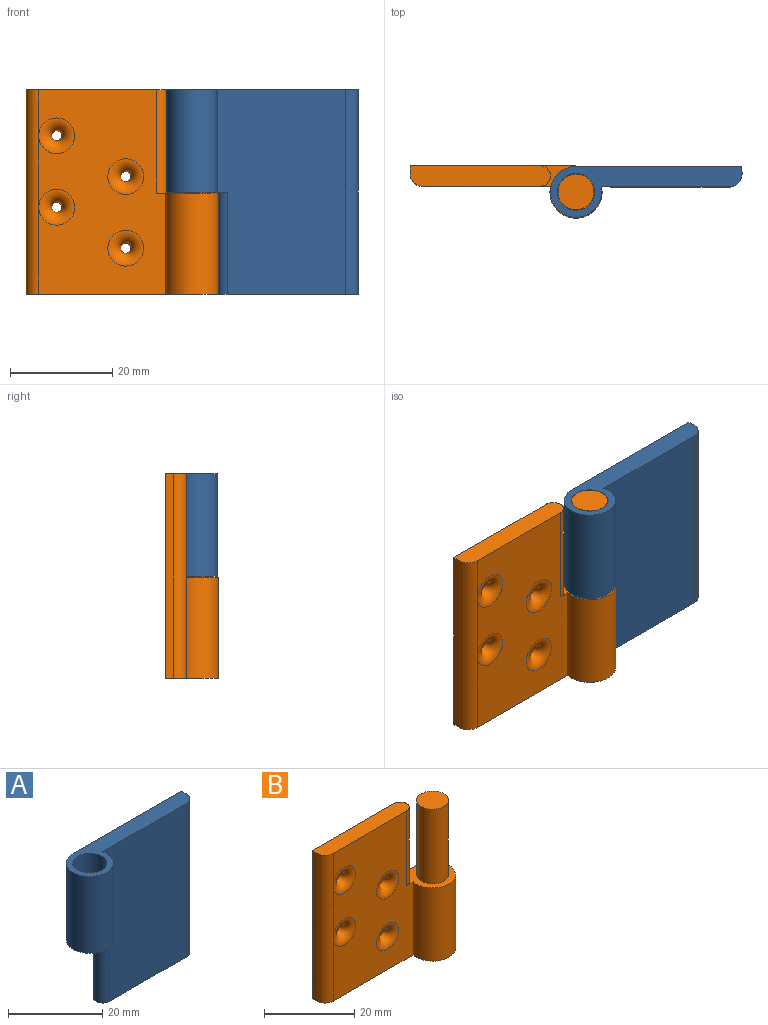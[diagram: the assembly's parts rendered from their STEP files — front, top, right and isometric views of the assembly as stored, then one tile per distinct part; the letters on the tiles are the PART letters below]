
ASSEMBLY  parts=2 mates=1
PART A: 10 faces, bbox 37.5x10x40 mm
  f0: plane 40x32.5mm, normal (0,1,0), area 1162mm2, adj f2,f3,f4,f5,f7,f8
  f1: plane 40x25.1mm, normal (0,-1,0), area 964mm2, adj f3,f4,f5,f7,f8,f9
  f2: plane 40x1.5mm, normal (1,0,0), area 60mm2, adj f0,f3,f4,f9
  f3: plane 37.5x10mm, normal (0,0,1), area 151.8mm2, adj f0,f1,f2,f5,f6,f9
  f4: plane 27.6x4mm, normal (0,0,-1), area 107.3mm2, adj f0,f1,f2,f8,f9
  f5: cylinder r=5mm len=20mm, axis (0,0,-1), area 491.4mm2, adj f0,f1,f3,f7
  f6: cylinder r=3.6mm len=20mm, axis (0,0,-1), area 452.4mm2, adj f3,f7
  f7: plane 11.9x10mm, normal (0,0,-1), area 44.5mm2, adj f0,f1,f5,f6,f8
  f8: cylinder r=2mm len=20mm, axis (0,0,1), area 125.7mm2, adj f0,f1,f4,f7
  f9: cylinder r=2.5mm len=40mm, axis (0,0,1), area 157.1mm2, adj f1,f2,f3,f4
PART B: 19 faces, bbox 37.6x10.2x40 mm
  f0: plane 40x1.5mm, normal (-1,0,0), area 60mm2, adj f2,f3,f4,f18
  f1: plane 40x25.02mm, normal (0,-1,0), area 806.5mm2, adj f3,f4,f5,f6,f9,f14,f15,f16
  f2: plane 40x32.5mm, normal (0,1,0), area 1146.4mm2, adj f0,f3,f4,f5,f6,f9,f10,f11
  f3: plane 27.52x4mm, normal (0,0,1), area 107mm2, adj f0,f1,f2,f9,f18
  f4: plane 37.6x10.2mm, normal (0,0,-1), area 195.5mm2, adj f0,f1,f2,f5,f18
  f5: cylinder r=5.1mm len=19.8mm, axis (0,0,-1), area 497.8mm2, adj f1,f2,f4,f6
  f6: plane 12.08x10.2mm, normal (0,0,1), area 50mm2, adj f1,f2,f5,f8,f9
  f7: plane 7x7mm, normal (0,0,1), area 38.5mm2, adj f8
  f8: cylinder r=3.5mm len=20.2mm, axis (0,0,-1), area 444.2mm2, adj f6,f7
  f9: cylinder r=2mm len=20.2mm, axis (0,0,-1), area 126.9mm2, adj f1,f2,f3,f6
  f10: cylinder r=1mm len=2mm, axis (0,-1,0), area 9.4mm2, adj f2,f14
  f11: cylinder r=1mm len=2mm, axis (0,-1,0), area 9.4mm2, adj f2,f15
  f12: cylinder r=1mm len=2mm, axis (0,-1,0), area 9.4mm2, adj f2,f16
  f13: cylinder r=1mm len=2mm, axis (0,-1,0), area 9.4mm2, adj f2,f17
  f14: torus R=3.5mm, axis (0,1,0), area 47.1mm2, adj f1,f10
  f15: torus R=3.5mm, axis (0,1,0), area 47.1mm2, adj f1,f11
  f16: torus R=3.5mm, axis (0,1,0), area 47.1mm2, adj f1,f12
  f17: torus R=3.5mm, axis (0,1,0), area 47.1mm2, adj f1,f13
  f18: cylinder r=2.5mm len=40mm, axis (0,0,-1), area 157.1mm2, adj f0,f1,f3,f4
PLACE A rot(axis=(0,0,1),0deg) t=(-123.74,-15.04,19.54)mm
PLACE B t=(-104.39,-8.37,19.54)mm
MATE cylindrical A.f5 <-> B.f5  axis (0,0,-1) through (-113.44,-18.56,39.54)mm
